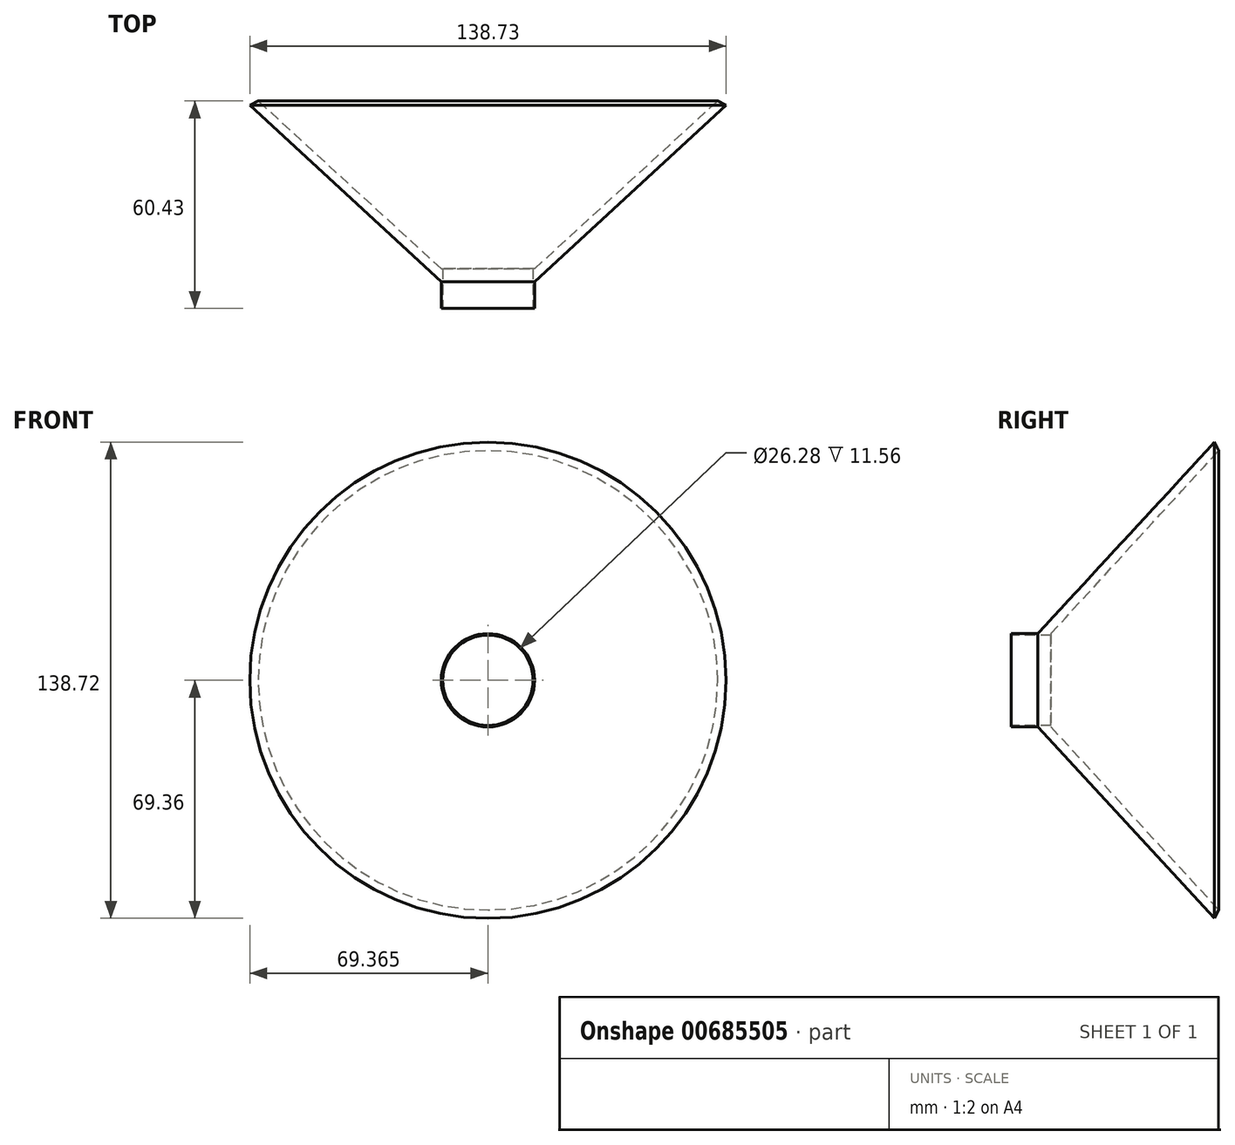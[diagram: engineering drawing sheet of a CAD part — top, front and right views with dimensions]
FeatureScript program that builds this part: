
annotation { "Feature Type Name" : "Feature", "Feature Type Description" : "" }
export const myFeature = defineFeature(function(context is Context, id is Id, definition is map)
    precondition{}
    {
        {
            var Q0;
            Q0=qCreatedBy(makeId("Top.planeOp"),FACE);
            var sketch = newSketch(context, id + "F0", { "sketchPlane" : qUnion([Q0])});
            skLineSegment(sketch, "E0", {"start": v(24.03, 43.6) * mm, "end": v(-29.3, -5.27) * mm});
            skLineSegment(sketch, "E1", {"start": v(-29.3, -5.27) * mm, "end": v(-42.9, -5.27) * mm});
            skLineSegment(sketch, "E2", {"start": v(-42.9, -5.27) * mm, "end": v(-42.9, -16.83) * mm});
            skLineSegment(sketch, "E3", {"start": v(-42.9, -16.83) * mm, "end": v(-29.3, -16.83) * mm});
            skLineSegment(sketch, "E4", {"start": v(-29.3, -16.83) * mm, "end": v(-29.3, -9.13) * mm});
            skLineSegment(sketch, "E5", {"start": v(-29.3, -9.13) * mm, "end": v(26.47, 42.39) * mm});
            skLineSegment(sketch, "E6", {"start": v(26.47, 42.39) * mm, "end": v(24.03, 43.6) * mm});
            skSolve(sketch);
        }
        {
            var Q0;
            Q0 = qSketchRegion(id + "F0", true);
            var Q1;
            Q1=sQuery(id+"F0.wireOp",EDGE,"E2");
            revolve(context, id + "F1", {"surfaceOperationType" : NewSurfaceOperationType.NEW, "entities" : qUnion([Q0]), "axis" : qUnion([Q1]), "revolveType" : RevolveType.FULL});
        }
        {
            var Q0;
            Q0=makeQuery(id+"F1.opRevolve","SWEPT_FACE",FACE,{"disambiguationData":[OSD([sQuery(id+"F0.wireOp",EDGE,"E3")])]});
            var sketch = newSketch(context, id + "F2", { "sketchPlane" : qUnion([Q0])});
            skCircle(sketch, "E7", {"center": v(-42.9, 0) * mm, "radius": 13.14 * mm});
            skSolve(sketch);
        }
        {
            var Q0;
            Q0=makeQuery(id+"F2.imprint","IMPRINT",FACE,{"disambiguationData":[TD([[makeQuery(id+"F2.imprint","IMPRINT",EDGE,{"derivedFrom":sQuery(id+"F2.wireOp",EDGE,"E7")}),1.0]])]});
            extrude(context, id + "F3", {"entities" : qUnion([Q0]), "operationType" : NewBodyOperationType.REMOVE, "oppositeDirection" : true, "depth" : 25.4 * mm, "offsetDistance" : 25.4 * mm});
        }
    });
